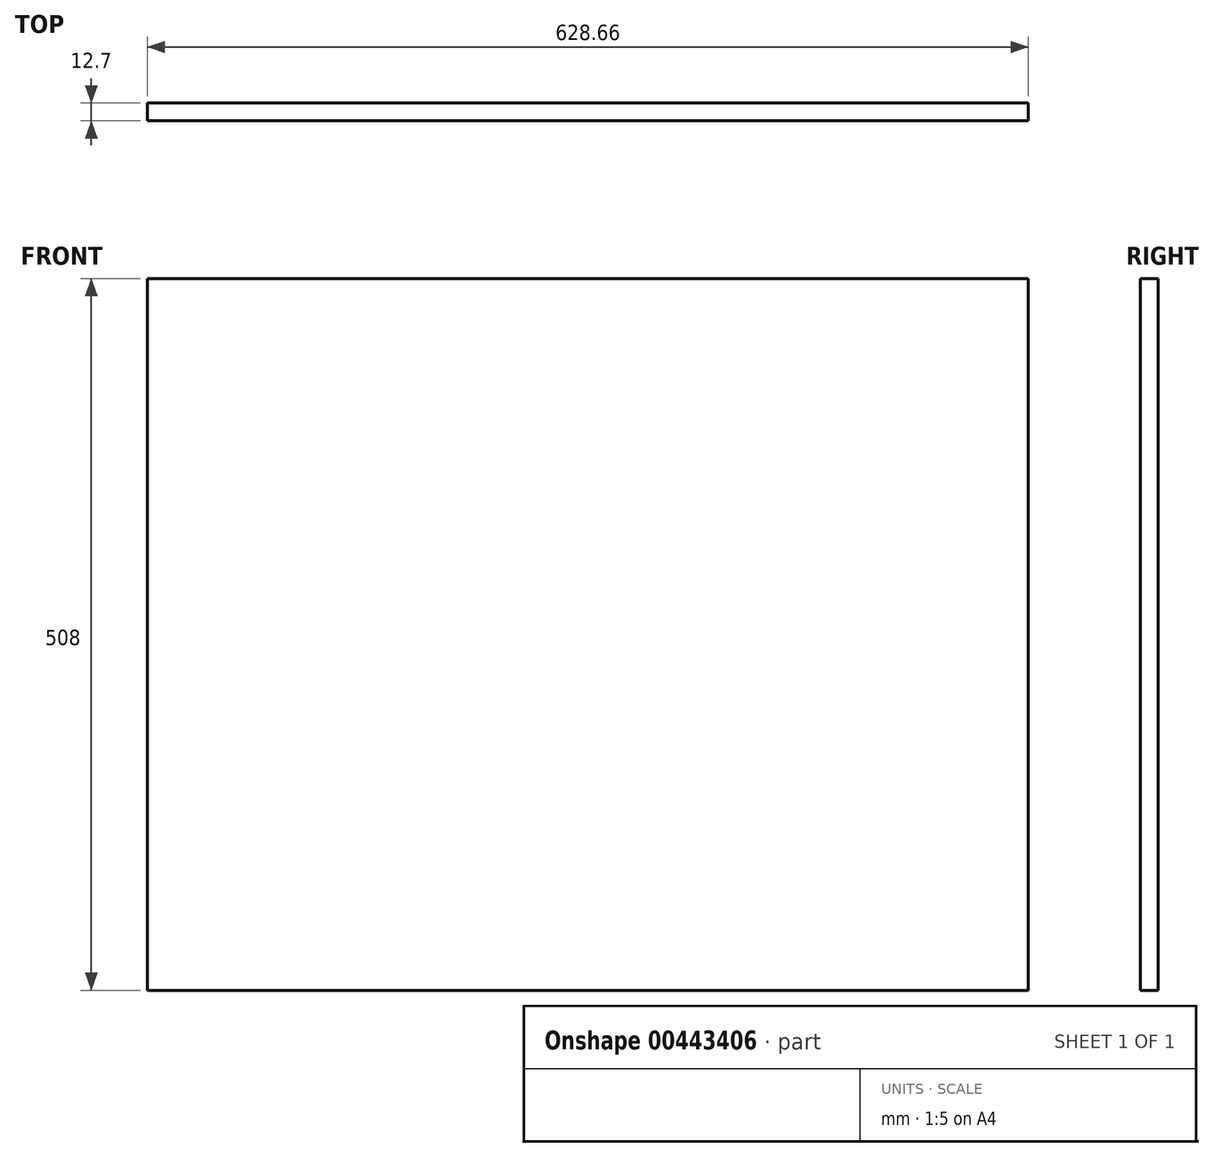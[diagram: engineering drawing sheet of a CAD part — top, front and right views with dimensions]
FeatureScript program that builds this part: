
annotation { "Feature Type Name" : "Feature", "Feature Type Description" : "" }
export const myFeature = defineFeature(function(context is Context, id is Id, definition is map)
    precondition{}
    {
        {
            var Q0;
            Q0=qCreatedBy(makeId("Front.planeOp"),FACE);
            var sketch = newSketch(context, id + "F0", { "sketchPlane" : qUnion([Q0])});
            skLineSegment(sketch, "E0.bottom", {"start": v(314.33, 254) * mm, "end": v(-314.32, 254) * mm});
            skLineSegment(sketch, "E0.top", {"start": v(314.32, -254) * mm, "end": v(-314.33, -254) * mm});
            skLineSegment(sketch, "E0.left", {"start": v(314.33, 254) * mm, "end": v(314.32, -254) * mm});
            skLineSegment(sketch, "E0.right", {"start": v(-314.32, 254) * mm, "end": v(-314.33, -254) * mm});
            skPoint(sketch, "E0.middle", {"position": v(0, 0) * mm});
            skSolve(sketch);
        }
        {
            var Q0;
            Q0 = qSketchRegion(id + "F0", true);
            extrude(context, id + "F1", {"entities" : qUnion([Q0]), "depth" : 12.7 * mm});
        }
    });
